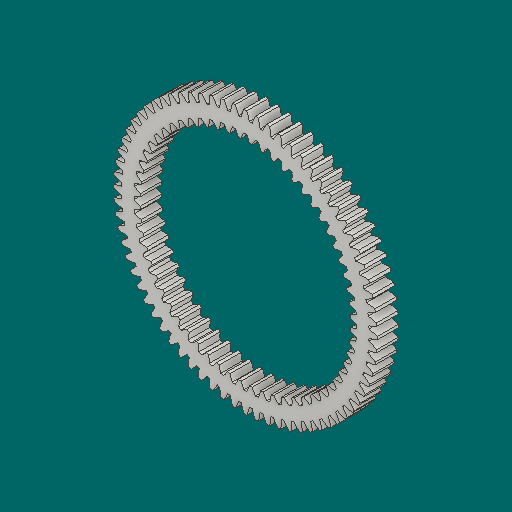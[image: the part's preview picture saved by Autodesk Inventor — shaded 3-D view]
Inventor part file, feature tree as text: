
AUTODESK INVENTOR PART (.ipt)
format: ipt  version: 2023.1 (Build 271208000, 208)  size: 846,848 bytes
history: native  units: mm (DEFAULTED — no unit token found)
features: other x6, plane x3, sketch x3, extrude x2, boolean_combine x1
ambient origin geometry x8: Origin, YZ Plane, XZ Plane, XY Plane, X Axis, Y Axis, Z Axis, Center Point
bodies: Solid1 (feature_tree), Solid1_1 (feature_tree)
feature tree (15):
  other  "Spur Gear2"
  extrude  "Extrusion1"  Depth=7.62mm TaperAngle=0.0deg
  plane  "Work Plane1"
  plane  "Work Plane2"
  plane  "Work Plane3"
  other  "Spur Gear"
  extrude  "Extrusion2"  Depth=76.2mm TaperAngle=0.0deg
  boolean_combine  "Combine1"
  sketch  "Sketch1"  dims[d0=93.98mm d1=7.62mm d2=0.0mm]
  sketch  "Sketch2"  dims[d3=91.44mm d4=76.2mm d5=0.0mm]
  other  "Srf1"
  sketch  "Sketch3"  dims[d6=0.0mm d7=0.436332mm d9=0.0mm d14=0.0mm d15=91.44mm d16=0.0mm d17=0.0mm d18=0.0mm d19=91.44mm d20=83.82mm d21=0.0mm d22=0.0mm d23=10.0mm]
  other  "Solid1::Spur Gear2"
  other  "TaggingFeature1"
  other  "Pitch Diameter"
